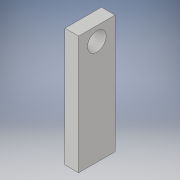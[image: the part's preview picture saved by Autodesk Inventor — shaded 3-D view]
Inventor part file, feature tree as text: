
AUTODESK INVENTOR PART (.ipt)
format: ipt  version: 2019 (Build 230136000, 136)  size: 112,128 bytes
history: native  units: in
note: dims shown in document units (in); Inventor stores cm internally (conversion verified against a paired STEP export)
features: sketch x2, extrude x1, hole x1, projected_geometry x1
ambient origin geometry x8: Origin, YZ Plane, XZ Plane, XY Plane, X Axis, Y Axis, Z Axis, Center Point
bodies: Solid1 (feature_tree)
feature tree (5):
  extrude  "Extrusion1"  Depth=1.0in
  hole  "Hole1"  [1 undecoded]
  sketch  "Sketch1"  dims[d0=3.25in d1=1.0in]
  sketch  "Sketch2"  dims[d2=0.51in d3=2.875in d4=0.375in d5=0.0in d6=1.0in d7=0.125in d8=0.125in d9=0.104in d10=0.276in d11=0.375in d12=0.25in d13=0.5635in d14=1.0in d15=0.8108in]
  projected_geometry  "Projected Loop1"
note: 1 required parameter value undecoded (feature->parameter linkage not recoverable at this tier; creation-order binding heuristic only, values carry confidence <= 0.55)
